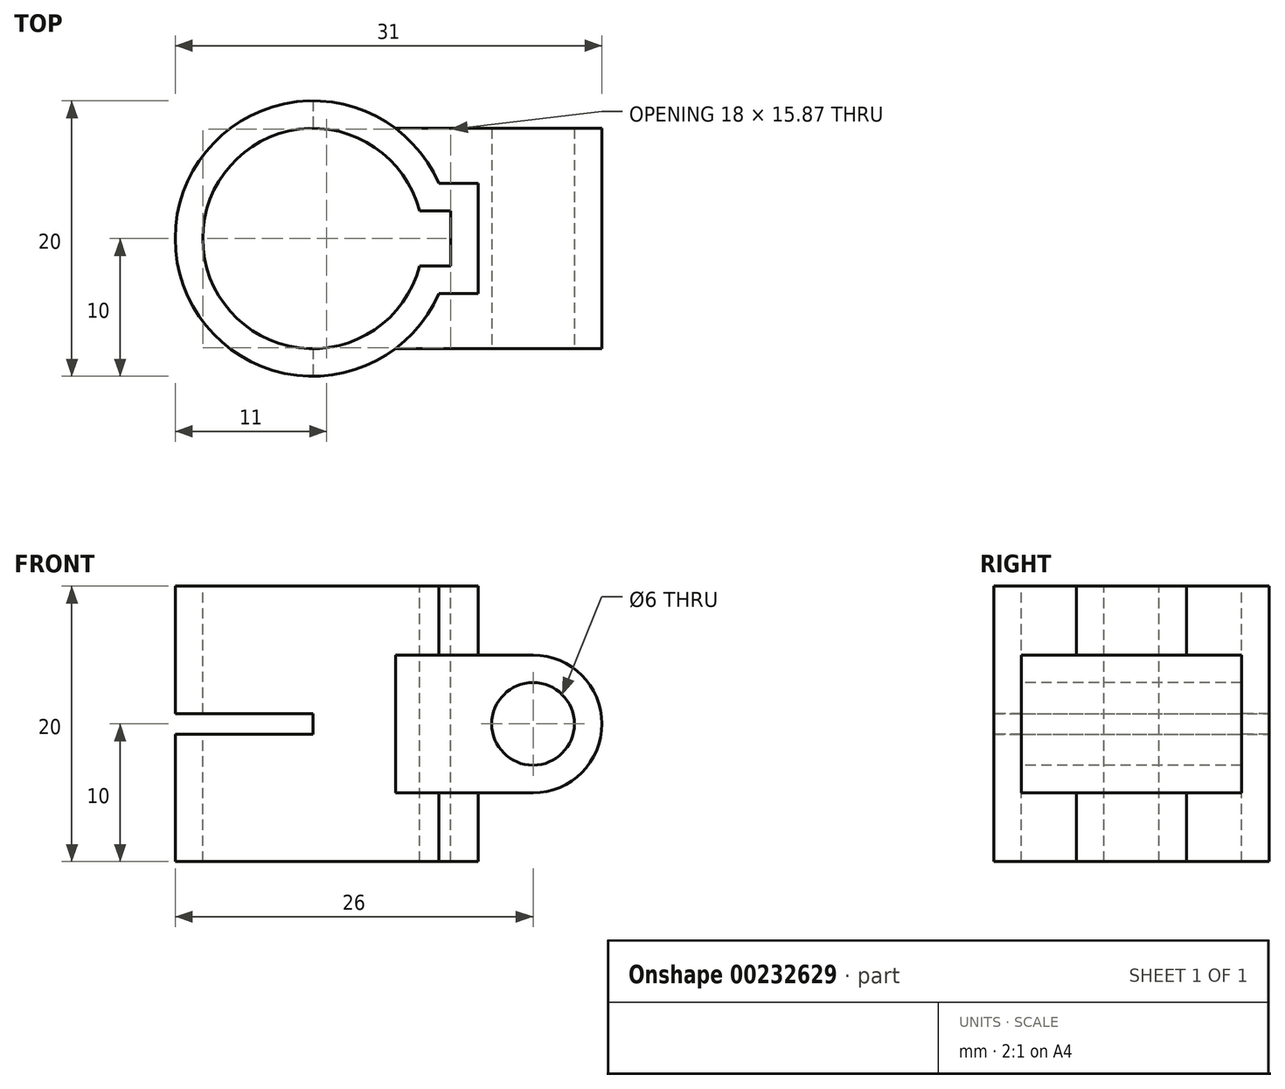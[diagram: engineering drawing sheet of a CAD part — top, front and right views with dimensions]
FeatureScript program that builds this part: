
annotation { "Feature Type Name" : "Feature", "Feature Type Description" : "" }
export const myFeature = defineFeature(function(context is Context, id is Id, definition is map)
    precondition{}
    {
        {
            var Q0;
            Q0=qCreatedBy(makeId("Top.planeOp"),FACE);
            var sketch = newSketch(context, id + "F0", { "sketchPlane" : qUnion([Q0])});
            skArc(sketch, "E0", {"start": v(9.17, 4) * mm, "mid": v(-10, 0) * mm, "end": v(9.17, -4) * mm});
            skLineSegment(sketch, "E1", {"start": v(9.17, 4) * mm, "end": v(12, 4) * mm});
            skLineSegment(sketch, "E2.MirrorCS", {"start": v(9.17, -4) * mm, "end": v(12, -4) * mm});
            skLineSegment(sketch, "E3", {"start": v(12, 4) * mm, "end": v(12, -4) * mm});
            skPoint(sketch, "E4.orphan", {"position": v(19.93, 4) * mm});
            skPoint(sketch, "E5.orphan", {"position": v(19.93, -4) * mm});
            skPoint(sketch, "E6.orphan", {"position": v(5.82, -4) * mm});
            skPoint(sketch, "E7.orphan", {"position": v(5.82, 4) * mm});
            skSolve(sketch);
        }
        {
            var Q0;
            Q0 = qSketchRegion(id + "F0", true);
            extrude(context, id + "F1", {"entities" : qUnion([Q0]), "depth" : 10 * mm, "hasSecondDirection" : true, "secondDirectionOppositeDirection" : true, "secondDirectionDepth" : 10 * mm});
        }
        {
            var Q0;
            Q0=qCreatedBy(makeId("Front.planeOp"),FACE);
            var sketch = newSketch(context, id + "F2", { "sketchPlane" : qUnion([Q0])});
            skLineSegment(sketch, "E8", {"start": v(0, 5) * mm, "end": v(0, -5) * mm});
            skLineSegment(sketch, "E9", {"start": v(0, 5) * mm, "end": v(16, 5) * mm});
            skLineSegment(sketch, "E10.MirrorCS", {"start": v(0, -5) * mm, "end": v(16, -5) * mm});
            skLineSegment(sketch, "E11", {"start": v(21, 0) * mm, "end": v(21, -5) * mm, "construction": true});
            skArc(sketch, "E12", {"start": v(16, -5) * mm, "mid": v(21, 0) * mm, "end": v(16, 5) * mm});
            skPoint(sketch, "E13.orphan", {"position": v(-8.75, 5) * mm});
            skPoint(sketch, "E14.orphan", {"position": v(-8.75, -5) * mm});
            skPoint(sketch, "E15.orphan", {"position": v(0, 10.9) * mm});
            skSolve(sketch);
        }
        {
            var Q0;
            Q0 = qSketchRegion(id + "F2", true);
            extrude(context, id + "F3", {"entities" : qUnion([Q0]), "operationType" : NewBodyOperationType.ADD, "depth" : 8 * mm, "hasSecondDirection" : true, "secondDirectionOppositeDirection" : true, "secondDirectionDepth" : 8 * mm});
        }
        {
            var Q0;
            Q0=makeQuery(id+"F1.opExtrude","CAP_FACE",FACE,{"disambiguationData":[OSD([sQuery(id+"F0.wireOp",EDGE,"E0"),sQuery(id+"F0.wireOp",EDGE,"E1"),sQuery(id+"F0.wireOp",EDGE,"E2.MirrorCS"),sQuery(id+"F0.wireOp",EDGE,"E3")])],"isStart":false});
            var sketch = newSketch(context, id + "F4", { "sketchPlane" : qUnion([Q0])});
            skArc(sketch, "E16.0", {"start": v(7.75, 2) * mm, "mid": v(-8, 0) * mm, "end": v(7.75, -2) * mm});
            skLineSegment(sketch, "E16.1", {"start": v(7.75, 2) * mm, "end": v(10, 2) * mm});
            skLineSegment(sketch, "E16.2", {"start": v(10, 2) * mm, "end": v(10, -2) * mm});
            skLineSegment(sketch, "E16.3", {"start": v(7.75, -2) * mm, "end": v(10, -2) * mm});
            skSolve(sketch);
        }
        {
            var Q0;
            Q0 = qSketchRegion(id + "F4", true);
            extrude(context, id + "F5", {"entities" : qUnion([Q0]), "operationType" : NewBodyOperationType.REMOVE, "endBound" : BoundingType.THROUGH_ALL, "oppositeDirection" : true, "depth" : 25 * mm});
        }
        {
            var Q0;
            Q0=makeQuery(id+"F3.opExtrude","CAP_FACE",FACE,{"disambiguationData":[OSD([sQuery(id+"F2.wireOp",EDGE,"E8"),sQuery(id+"F2.wireOp",EDGE,"E9"),sQuery(id+"F2.wireOp",EDGE,"E10.MirrorCS"),sQuery(id+"F2.wireOp",EDGE,"E12")])],"isStart":false});
            var sketch = newSketch(context, id + "F6", { "sketchPlane" : qUnion([Q0])});
            skCircle(sketch, "E17", {"center": v(16, 0) * mm, "radius": 3 * mm});
            skSolve(sketch);
        }
        {
            var Q0;
            Q0 = qSketchRegion(id + "F6", true);
            extrude(context, id + "F7", {"entities" : qUnion([Q0]), "operationType" : NewBodyOperationType.REMOVE, "endBound" : BoundingType.THROUGH_ALL, "oppositeDirection" : true, "depth" : 25 * mm});
        }
        {
            var Q0;
            Q0=qCreatedBy(makeId("Front.planeOp"),FACE);
            var sketch = newSketch(context, id + "F8", { "sketchPlane" : qUnion([Q0])});
            skLineSegment(sketch, "E18.bottom", {"start": v(-12, 0.75) * mm, "end": v(0, 0.75) * mm});
            skLineSegment(sketch, "E18.top", {"start": v(-12, -0.75) * mm, "end": v(0, -0.75) * mm});
            skLineSegment(sketch, "E18.left", {"start": v(-12, 0.75) * mm, "end": v(-12, -0.75) * mm});
            skLineSegment(sketch, "E18.right", {"start": v(0, 0.75) * mm, "end": v(0, -0.75) * mm});
            skSolve(sketch);
        }
        {
            var Q0;
            Q0 = qSketchRegion(id + "F8", true);
            extrude(context, id + "F9", {"entities" : qUnion([Q0]), "operationType" : NewBodyOperationType.REMOVE, "endBound" : BoundingType.THROUGH_ALL, "oppositeDirection" : true, "depth" : 25 * mm, "hasSecondDirection" : true, "secondDirectionBound" : SecondDirectionBoundingType.THROUGH_ALL, "secondDirectionOppositeDirection" : false, "secondDirectionDepth" : 25 * mm});
        }
    });
